# Revit family: Lighting_Fixture-Wall-Astro-Kashimaxxx
name_source: partatom
category: Lighting Fixtures
revit_build: Autodesk Revit LT 2014 (Build: 20130308_1515(x64)
units: mm (PartAtom-declared; Revit-internal decimal feet)

## types (2) — shared parameters
Assembly Code = D5020200
Backplate Material = Astro - Zinc - Chrome Finish
Casing Material = Astro - Aluminium - Polished Chrome
Class = 2
Color Filter = 16777215
Description = Mirror Light
Dimmable = No
Dimming Lamp Color Temperature Shift = <None>
Height = 45 mm  [stored 0.147638 ft]
IP Rating = IP44
Lamp = T5
Lamp included = Yes
Length = 192 mm  [stored 0.629921 ft]
Light Source From Wall = 177.5 mm
Manufacturer = Astro Lighting Ltd, CM20 2DP
Mountable on normally flammable surfaces = Yes
Number of Poles = 1
Product Documentation = http://www.astrolighting.co.uk
Suitable for bathroom zone = Zones 2 and 3
URL = www.astrolighting.co.uk
Voltage = 230 V

## per-type parameters (varying)
| type | Aperture Width | Apparent Load | Arm Height | Emit from Line Length | Energy Efficiency Rating | Luminaire Lamp Efficiency Rating | Photometric Web File | Tilt Angle | Type Comments | Wattage Comments | Weight | Width |
| 0814 Kashima | 254 mm | 9 VA | 9.5 mm  [stored 0.031168 ft] | 300 mm | A | A-B | 0814 KASHIMA.ies | -90.00° | Includes integral electronic ballast. Comes with wall and cabinet mounting brackets. | 8w | 1.5kg | 350 mm  [stored 1.14829 ft] |
| 0961 Kashima 620 | 505 mm  [stored 1.65682 ft] | 16 VA | 10 mm  [stored 0.0328084 ft] | 565 mm  [stored 1.85367 ft] |  | A | 0961 KASHIMA 620.ies | 90.00° | Includes integral electronic ballast. Also supplied with an optional cabinet fixing bracket. | 14w | 1.75kg | 620 mm  [stored 2.03412 ft] |

note: column(s) folded — value = type name in every type: Model

note: [stored X ft] marks values corroborated as IEEE doubles in the binary element streams (Revit-internal decimal feet)

## geometry (parser evidence)
native form markers: Sweep x1
no freeform markers — native parametric forms only
